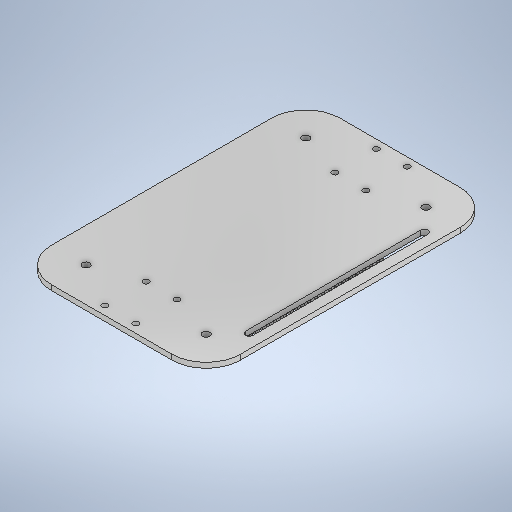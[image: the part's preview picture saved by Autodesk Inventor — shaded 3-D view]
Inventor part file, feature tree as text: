
AUTODESK INVENTOR PART (.ipt)
format: ipt  version: 2025.2 (Build 292293000, 293)  size: 376,832 bytes
history: native  units: mm
features: sketch x4, extrude x3, plane x3, hole x2, fillet x1, pattern_linear x1
ambient origin geometry x8: Origin, YZ Plane, XZ Plane, XY Plane, X Axis, Y Axis, Z Axis, Center Point
bodies: Solid1 (feature_tree)
feature tree (14):
  sketch  "Sketch1"  dims[d4=110.0mm d5=168.0mm]
  extrude  "Extrusion2"  Depth=168.0mm
  hole  "Hole1"  [1 undecoded]
  fillet  "Fillet1"  Radius=18.0mm
  plane  "Work Plane1"
  plane  "Work Plane2"
  hole  "Hole2"  [1 undecoded]
  extrude  "Extrusion3"  Depth=24.0mm
  plane  "Work Plane3"
  extrude  "Extrusion4"  Depth=20.0mm
  pattern_linear  "Rectangular Pattern1"  Spacing1=-84.0mm  [1 undecoded]
  sketch  "Sketch2"  dims[d20=3.0mm d21=0.0mm d22=5.0mm d23=18.0mm]
  sketch  "Sketch4"  dims[d24=24.0mm d25=5.0mm]
  sketch  "Sketch5"  dims[d26=18.0mm d27=24.0mm d28=3.4mm d29=6.0mm d30=4.0mm d31=2.0mm d32=90.0deg d33=8.0mm d34=20.594885mm d35=20.0mm d36=-84.0mm d37=-55.0mm d38=4.3mm d39=6.0mm d40=4.0mm d41=2.0mm d42=90.0deg d43=8.0mm d44=20.594885mm d45=8.0mm d46=102.0mm d47=8.0mm d48=4.3mm d49=0.0mm d50=0.0mm d51=5.0mm d52=2.0mm d53=85.0mm d54=5.0mm d55=17.0mm d56=0.0mm d57=230.0mm d59=4.0mm]
note: 3 required parameter values undecoded (feature->parameter linkage not recoverable at this tier; creation-order binding heuristic only, values carry confidence <= 0.55)
